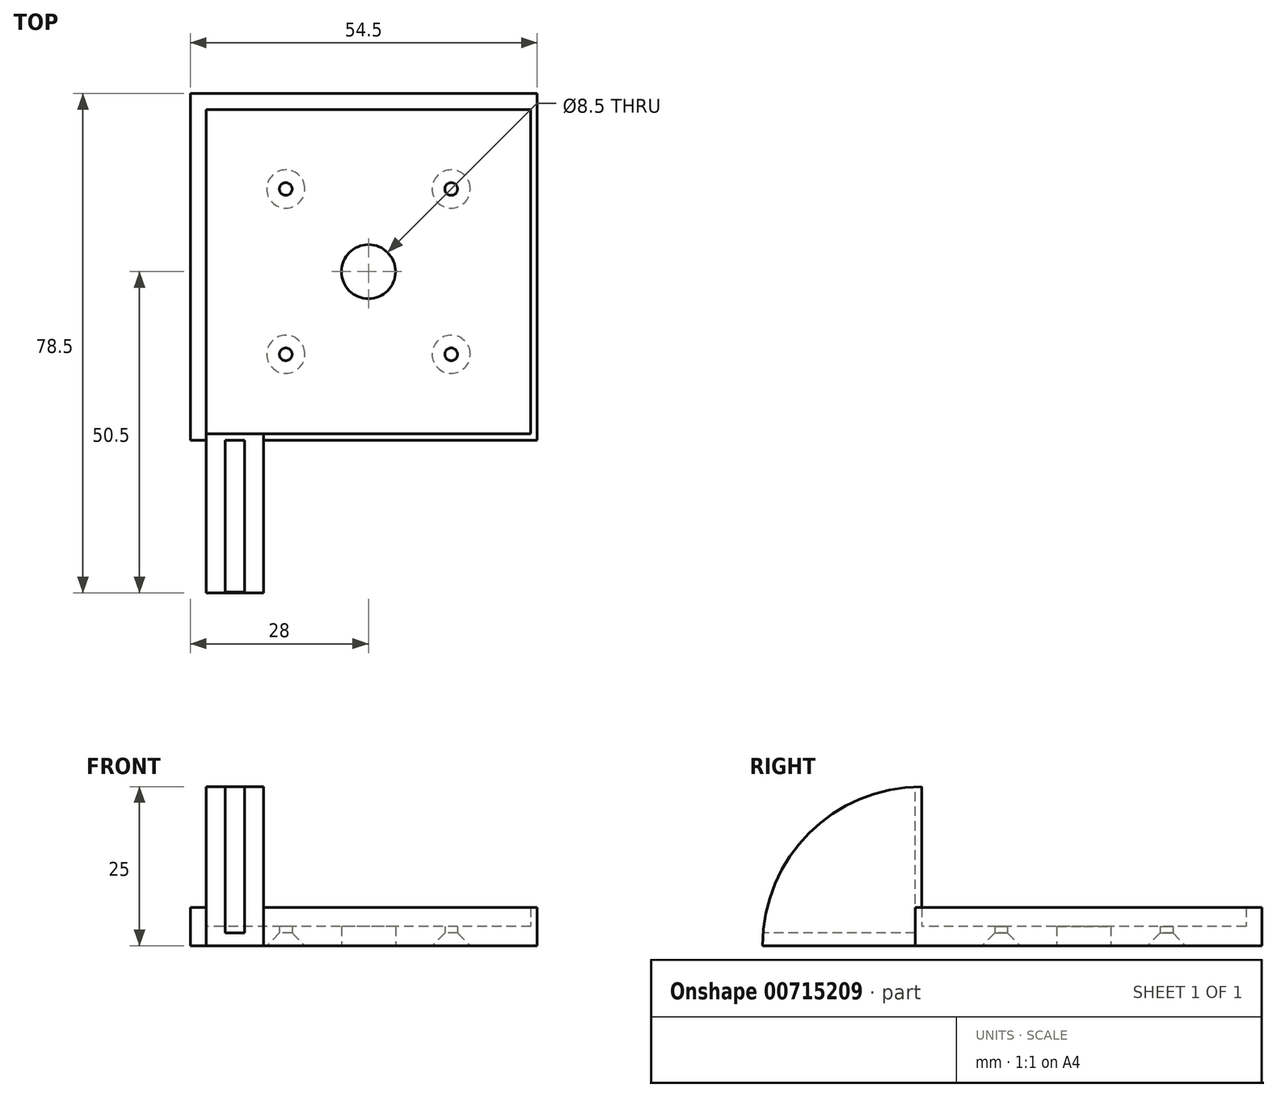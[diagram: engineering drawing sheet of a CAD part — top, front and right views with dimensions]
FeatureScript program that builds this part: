
annotation { "Feature Type Name" : "Feature", "Feature Type Description" : "" }
export const myFeature = defineFeature(function(context is Context, id is Id, definition is map)
    precondition{}
    {
        {
            var Q0;
            Q0=qCreatedBy(makeId("Top.planeOp"),FACE);
            var sketch = newSketch(context, id + "F0", { "sketchPlane" : qUnion([Q0])});
            skLineSegment(sketch, "E0.bottom", {"start": v(25.5, 25.5) * mm, "end": v(-25.5, 25.5) * mm});
            skLineSegment(sketch, "E0.top", {"start": v(25.5, -25.5) * mm, "end": v(-22.25, -25.5) * mm});
            skLineSegment(sketch, "E0.left", {"start": v(25.5, 25.5) * mm, "end": v(25.5, -25.5) * mm});
            skLineSegment(sketch, "E0.right", {"start": v(-25.5, 25.5) * mm, "end": v(-25.5, -25.5) * mm});
            skPoint(sketch, "E0.middle", {"position": v(0, 0) * mm});
            skLineSegment(sketch, "E1.0", {"start": v(28, 28) * mm, "end": v(-28, 28) * mm});
            skLineSegment(sketch, "E1.1", {"start": v(28, 28) * mm, "end": v(28, -28) * mm});
            skLineSegment(sketch, "E1.2", {"start": v(28, -28) * mm, "end": v(-22.25, -28) * mm});
            skLineSegment(sketch, "E1.3", {"start": v(-28, 28) * mm, "end": v(-28, -28) * mm});
            skCircle(sketch, "E2", {"center": v(-13, 13) * mm, "radius": 1 * mm});
            skLineSegment(sketch, "E3", {"start": v(0, 28) * mm, "end": v(0, -28) * mm, "construction": true});
            skLineSegment(sketch, "E4", {"start": v(-28, 0) * mm, "end": v(28, 0) * mm, "construction": true});
            skCircle(sketch, "E5.MirrorC", {"center": v(13, 13) * mm, "radius": 1 * mm});
            skCircle(sketch, "E6.MirrorC", {"center": v(13, -13) * mm, "radius": 1 * mm});
            skCircle(sketch, "E7.MirrorC", {"center": v(-13, -13) * mm, "radius": 1 * mm});
            skLineSegment(sketch, "E8.1", {"start": v(28, 30) * mm, "end": v(-30, 30) * mm});
            skLineSegment(sketch, "E9", {"start": v(28, 30) * mm, "end": v(28, 28) * mm});
            skLineSegment(sketch, "E10", {"start": v(-28, -28) * mm, "end": v(-30, -28) * mm});
            skLineSegment(sketch, "E11", {"start": v(28, 23.2) * mm, "end": v(28, 12.96) * mm});
            skLineSegment(sketch, "E12", {"start": v(28, 23.2) * mm, "end": v(28, 20) * mm});
            skLineSegment(sketch, "E13.trimOffspring", {"start": v(-25.25, -28) * mm, "end": v(-28, -28) * mm});
            skLineSegment(sketch, "E14", {"start": v(-25.5, -25.5) * mm, "end": v(-22.25, -25.5) * mm});
            skLineSegment(sketch, "E15", {"start": v(-25.25, -28) * mm, "end": v(-22.25, -28) * mm});
            skCircle(sketch, "E16", {"center": v(0, 0) * mm, "radius": 4.25 * mm});
            skLineSegment(sketch, "E17", {"start": v(-30, 30) * mm, "end": v(-30, -28) * mm});
            skSolve(sketch);
        }
        {
            var Q0;
            Q0=qCreatedBy(makeId("Top.planeOp"),FACE);
            var sketch = newSketch(context, id + "F1", { "sketchPlane" : qUnion([Q0])});
            skPoint(sketch, "E18.0", {"position": v(-25.5, -25.5) * mm});
            skLineSegment(sketch, "E19.bottom", {"start": v(-25.5, -25.5) * mm, "end": v(-16.5, -25.5) * mm});
            skLineSegment(sketch, "E19.top", {"start": v(-25.5, -50.5) * mm, "end": v(-16.5, -50.5) * mm});
            skLineSegment(sketch, "E19.left", {"start": v(-25.5, -25.5) * mm, "end": v(-25.5, -50.5) * mm});
            skLineSegment(sketch, "E19.right", {"start": v(-16.5, -25.5) * mm, "end": v(-16.5, -50.5) * mm});
            skLineSegment(sketch, "E20", {"start": v(-21, -50.5) * mm, "end": v(-21, -25.5) * mm, "construction": true});
            skLineSegment(sketch, "E21", {"start": v(-19.45, -25.5) * mm, "end": v(-19.45, -50.5) * mm});
            skLineSegment(sketch, "E22.MirrorCS", {"start": v(-22.55, -25.5) * mm, "end": v(-22.55, -50.5) * mm});
            skPoint(sketch, "E23.0", {"position": v(25.5, 25.5) * mm});
            skLineSegment(sketch, "E24.bottom", {"start": v(25.5, 25.5) * mm, "end": v(50.5, 25.5) * mm});
            skLineSegment(sketch, "E24.top", {"start": v(25.5, 16.5) * mm, "end": v(50.5, 16.5) * mm});
            skLineSegment(sketch, "E24.left", {"start": v(25.5, 25.5) * mm, "end": v(25.5, 16.5) * mm});
            skLineSegment(sketch, "E24.right", {"start": v(50.5, 25.5) * mm, "end": v(50.5, 16.5) * mm});
            skLineSegment(sketch, "E25", {"start": v(25.5, 21) * mm, "end": v(50.5, 21) * mm, "construction": true});
            skLineSegment(sketch, "E26", {"start": v(50.5, 22.55) * mm, "end": v(25.5, 22.55) * mm});
            skLineSegment(sketch, "E27.MirrorCS", {"start": v(50.5, 19.45) * mm, "end": v(25.5, 19.45) * mm});
            skSolve(sketch);
        }
        {
            var Q0;
            Q0=makeQuery(id+"F0.imprint","IMPRINT",FACE,{"disambiguationData":[TD([[makeQuery(id+"F0.imprint","IMPRINT",EDGE,{"derivedFrom":sQuery(id+"F0.wireOp",EDGE,"E0.bottom")}),1.0]])]});
            extrude(context, id + "F2", {"entities" : qUnion([Q0]), "depth" : 3 * mm, "offsetDistance" : 25 * mm});
        }
        {
            var Q0;
            Q0=makeQuery(id+"F0.imprint","IMPRINT",FACE,{"disambiguationData":[TD([[makeQuery(id+"F0.imprint","IMPRINT",EDGE,{"derivedFrom":sQuery(id+"F0.wireOp",EDGE,"E0.bottom")}),-1.0]])]});
            var Q1;
            {var subQ5=sQuery(id+"F0.wireOp",EDGE,"TI18WCdd-EPFC-hNpH-Rctt-afuqL8Zf6Xfq");Q1=makeQuery(id+"F0.imprint","IMPRINT",FACE,{"disambiguationData":[TD([[makeQuery(id+"F0.imprint","IMPRINT",EDGE,{"derivedFrom":subQ5}),-1.0]])]});}
            extrude(context, id + "F3", {"entities" : qUnion([Q0, Q1]), "operationType" : NewBodyOperationType.ADD, "depth" : 6 * mm, "offsetDistance" : 25 * mm});
        }
        {
            var Q0;
            Q0=makeQuery(id+"F2.opExtrude","CAP_EDGE",EDGE,{"disambiguationData":[OSD([sQuery(id+"F0.wireOp",EDGE,"E7.MirrorC")])],"isStart":true});
            var Q1;
            Q1=makeQuery(id+"F2.opExtrude","CAP_EDGE",EDGE,{"disambiguationData":[OSD([sQuery(id+"F0.wireOp",EDGE,"E6.MirrorC")])],"isStart":true});
            var Q2;
            Q2=makeQuery(id+"F2.opExtrude","CAP_EDGE",EDGE,{"disambiguationData":[OSD([sQuery(id+"F0.wireOp",EDGE,"E5.MirrorC")])],"isStart":true});
            var Q3;
            Q3=makeQuery(id+"F2.opExtrude","CAP_EDGE",EDGE,{"disambiguationData":[OSD([sQuery(id+"F0.wireOp",EDGE,"E2")])],"isStart":true});
            chamfer(context, id + "F4", {"entities" : qUnion([Q0, Q1, Q2, Q3]), "width" : 2 * mm, "tangentPropagation" : true});
        }
        {
            var Q0;
            Q0=makeQuery(id+"FIbiUBh41szAzK7_1.boolean.opBoolean","MERGE",FACE,{"derivedFrom":[makeQuery(id+"F3.opExtrude","SWEPT_FACE",FACE,{"disambiguationData":[OSD([sQuery(id+"F0.wireOp",EDGE,"E1.2"),sQuery(id+"F0.wireOp",EDGE,"E13.trimOffspring"),sQuery(id+"F0.wireOp",EDGE,"E15")])]}),makeQuery(id+"FIbiUBh41szAzK7_1.opExtrude","SWEPT_FACE",FACE,{"disambiguationData":[OSD([sQuery(id+"F0.wireOp",EDGE,"E10")])]})]});
            extrude(context, id + "F5", {"entities" : qUnion([Q0]), "operationType" : NewBodyOperationType.REMOVE, "oppositeDirection" : true, "depth" : 1.5 * mm, "offsetDistance" : 25 * mm});
        }
        {
            var Q0;
            Q0=makeQuery(id+"FIbiUBh41szAzK7_1.boolean.opBoolean","MERGE",FACE,{"derivedFrom":[makeQuery(id+"F3.opExtrude","SWEPT_FACE",FACE,{"disambiguationData":[OSD([sQuery(id+"F0.wireOp",EDGE,"E1.1"),sQuery(id+"F0.wireOp",EDGE,"E11"),sQuery(id+"F0.wireOp",EDGE,"E12")])]}),makeQuery(id+"FIbiUBh41szAzK7_1.opExtrude","SWEPT_FACE",FACE,{"disambiguationData":[OSD([sQuery(id+"F0.wireOp",EDGE,"E9")])]})]});
            extrude(context, id + "F6", {"entities" : qUnion([Q0]), "operationType" : NewBodyOperationType.REMOVE, "oppositeDirection" : true, "depth" : 1.5 * mm, "offsetDistance" : 25 * mm});
        }
        {
            var Q0;
            {var subQ0=sQuery(id+"F1.wireOp",EDGE,"E19.right");Q0=makeQuery(id+"F1.imprint","IMPRINT",FACE,{"disambiguationData":[TD([[makeQuery(id+"F1.imprint","IMPRINT",EDGE,{"derivedFrom":subQ0}),-1.0]])]});}
            var Q1;
            {var subQ0=sQuery(id+"F1.wireOp",EDGE,"E19.left");Q1=makeQuery(id+"F1.imprint","IMPRINT",FACE,{"disambiguationData":[TD([[makeQuery(id+"F1.imprint","IMPRINT",EDGE,{"derivedFrom":subQ0}),1.0]])]});}
            extrude(context, id + "F7", {"entities" : qUnion([Q0, Q1]), "operationType" : NewBodyOperationType.ADD, "depth" : 25 * mm, "offsetDistance" : 25 * mm});
        }
        {
            var Q0;
            {var subQ0=sQuery(id+"F1.wireOp",EDGE,"E21");Q0=makeQuery(id+"F1.imprint","IMPRINT",FACE,{"disambiguationData":[TD([[makeQuery(id+"F1.imprint","IMPRINT",EDGE,{"derivedFrom":subQ0}),-1.0]])]});}
            extrude(context, id + "F8", {"entities" : qUnion([Q0]), "operationType" : NewBodyOperationType.ADD, "depth" : 2 * mm, "offsetDistance" : 25 * mm});
        }
        {
            var Q0;
            {var subQ1=sQuery(id+"F1.wireOp",EDGE,"E21");var subQ3=sQuery(id+"F0.wireOp",EDGE,"E15");var subQ4=sQuery(id+"F0.wireOp",EDGE,"E13.trimOffspring");var subQ5=sQuery(id+"F0.wireOp",EDGE,"E1.2");var subQ6=sQuery(id+"F0.wireOp",EDGE,"E14");var subQ7=sQuery(id+"F0.wireOp",EDGE,"E0.top");Q0=makeQuery(id+"F7.boolean.opBoolean","SPLIT",FACE,{"disambiguationData":[TD([makeQuery(id+"F7.opExtrude","SWEPT_FACE",FACE,{"disambiguationData":[OSD([subQ1])]})])],"derivedFrom":makeQuery(id+"F3.opExtrude","CAP_FACE",FACE,{"disambiguationData":[OSD([sQuery(id+"F0.wireOp",EDGE,"E0.bottom"),subQ7,sQuery(id+"F0.wireOp",EDGE,"E0.left"),sQuery(id+"F0.wireOp",EDGE,"E0.right"),sQuery(id+"F0.wireOp",EDGE,"E1.0"),sQuery(id+"F0.wireOp",EDGE,"E1.1"),subQ5,sQuery(id+"F0.wireOp",EDGE,"E1.3"),sQuery(id+"F0.wireOp",EDGE,"E11"),sQuery(id+"F0.wireOp",EDGE,"E12"),subQ4,subQ6,subQ3])],"isStart":false})});}
            var Q1;
            {var subQ1=sQuery(id+"F1.wireOp",EDGE,"E26");var subQ2=sQuery(id+"F0.wireOp",EDGE,"E12");var subQ3=sQuery(id+"F0.wireOp",EDGE,"E11");var subQ4=sQuery(id+"F0.wireOp",EDGE,"E1.1");var subQ6=sQuery(id+"F0.wireOp",EDGE,"E0.left");Q1=makeQuery(id+"F7.boolean.opBoolean","SPLIT",FACE,{"disambiguationData":[TD([makeQuery(id+"F7.opExtrude","SWEPT_FACE",FACE,{"disambiguationData":[OSD([subQ1])]})])],"derivedFrom":makeQuery(id+"F3.opExtrude","CAP_FACE",FACE,{"disambiguationData":[OSD([sQuery(id+"F0.wireOp",EDGE,"E0.bottom"),sQuery(id+"F0.wireOp",EDGE,"E0.top"),subQ6,sQuery(id+"F0.wireOp",EDGE,"E0.right"),sQuery(id+"F0.wireOp",EDGE,"E1.0"),subQ4,sQuery(id+"F0.wireOp",EDGE,"E1.2"),sQuery(id+"F0.wireOp",EDGE,"E1.3"),subQ3,subQ2,sQuery(id+"F0.wireOp",EDGE,"E13.trimOffspring"),sQuery(id+"F0.wireOp",EDGE,"E14"),sQuery(id+"F0.wireOp",EDGE,"E15")])],"isStart":false})});}
            var Q2;
            Q2=makeQuery(id+"F7.opExtrude","CAP_FACE",FACE,{"disambiguationData":[OSD([sQuery(id+"F1.wireOp",EDGE,"E19.bottom"),sQuery(id+"F1.wireOp",EDGE,"E19.top"),sQuery(id+"F1.wireOp",EDGE,"E19.left"),sQuery(id+"F1.wireOp",EDGE,"E22.MirrorCS")])],"isStart":false});
            var Q3;
            Q3=makeQuery(id+"F2.opExtrude","SWEPT_BODY",BODY,{"disambiguationData":[OSD([sQuery(id+"F0.wireOp",EDGE,"E0.bottom"),sQuery(id+"F0.wireOp",EDGE,"E0.top"),sQuery(id+"F0.wireOp",EDGE,"E0.left"),sQuery(id+"F0.wireOp",EDGE,"E0.right"),sQuery(id+"F0.wireOp",EDGE,"E2"),sQuery(id+"F0.wireOp",EDGE,"E5.MirrorC"),sQuery(id+"F0.wireOp",EDGE,"E6.MirrorC"),sQuery(id+"F0.wireOp",EDGE,"E7.MirrorC"),sQuery(id+"F0.wireOp",EDGE,"E14"),sQuery(id+"F0.wireOp",EDGE,"E16")])]});
            extrude(context, id + "F9", {"entities" : qUnion([Q0, Q1]), "operationType" : NewBodyOperationType.ADD, "endBound" : BoundingType.UP_TO_SURFACE, "depth" : 25 * mm, "endBoundEntityFace" : qUnion([Q2]), "endBoundEntityBody" : qUnion([Q3]), "offsetDistance" : 25 * mm});
        }
        {
            var Q0;
            {var subQ0=sQuery(id+"F1.wireOp",EDGE,"E19.top");Q0=makeQuery(id+"F7.opExtrude","CAP_EDGE",EDGE,{"disambiguationData":[OSD([subQ0]),TDD([makeQuery(id+"F1.imprint","IMPRINT",EDGE,{"disambiguationData":[TD([[makeQuery(id+"F1.imprint","INTERSECT",VERTEX,{"derivedFrom":[subQ0,sQuery(id+"F1.wireOp",EDGE,"E19.left")]}),-1.0]])],"derivedFrom":subQ0})])],"isStart":false});}
            var Q1;
            {var subQ0=sQuery(id+"F1.wireOp",EDGE,"E19.top");Q1=makeQuery(id+"F7.opExtrude","CAP_EDGE",EDGE,{"disambiguationData":[OSD([subQ0]),TDD([makeQuery(id+"F1.imprint","IMPRINT",EDGE,{"disambiguationData":[TD([[makeQuery(id+"F1.imprint","INTERSECT",VERTEX,{"derivedFrom":[subQ0,sQuery(id+"F1.wireOp",EDGE,"E19.right")]}),1.0]])],"derivedFrom":subQ0})])],"isStart":false});}
            var Q2;
            {var subQ0=sQuery(id+"F1.wireOp",EDGE,"E24.right");Q2=makeQuery(id+"F7.opExtrude","CAP_EDGE",EDGE,{"disambiguationData":[OSD([subQ0]),TDD([makeQuery(id+"F1.imprint","IMPRINT",EDGE,{"disambiguationData":[TD([[makeQuery(id+"F1.imprint","INTERSECT",VERTEX,{"derivedFrom":[sQuery(id+"F1.wireOp",EDGE,"E24.bottom"),subQ0]}),-1.0]])],"derivedFrom":subQ0})])],"isStart":false});}
            fillet(context, id + "F10", {"entities" : qUnion([Q0, Q1, Q2]), "radius" : 25 * mm, "tangentPropagation" : true, "allowEdgeOverflow" : false});
        }
    });
